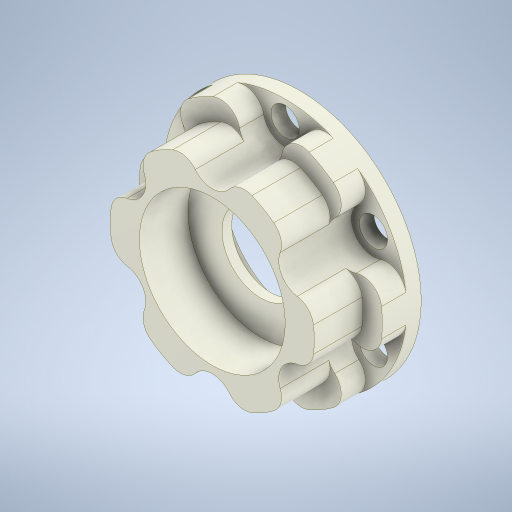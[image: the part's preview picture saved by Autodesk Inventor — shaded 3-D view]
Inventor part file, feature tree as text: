
AUTODESK INVENTOR PART (.ipt)
format: ipt  version: 2023.1 (Build 271208000, 208)  size: 422,400 bytes
history: native  units: mm
features: sketch x7, extrude x6, hole x1, fillet x1, pattern_circular x1
ambient origin geometry x8: Origin, YZ Plane, XZ Plane, XY Plane, X Axis, Y Axis, Z Axis, Center Point
bodies: Solid1 (feature_tree)
feature tree (16):
  extrude  "Extrusion1"  Depth=9.5mm TaperAngle=0.0deg
  hole  "Hole1"  [1 undecoded]
  extrude  "Extrusion2"  Depth=9.5mm
  extrude  "Extrusion3"  Depth=3.0mm
  extrude  "Extrusion4"  Depth=5.5mm TaperAngle=0.0deg
  extrude  "Extrusion5"  TaperAngle=0.0deg  [1 undecoded]
  fillet  "Fillet1"  Radius=2.0mm
  pattern_circular  "Circular Pattern1"  Count=6 Angle=360.0deg
  extrude  "Extrusion6"  [1 undecoded]
  sketch  "Sketch1"  dims[d0=25.0mm d1=9.5mm d2=0.0mm]
  sketch  "Sketch2"  dims[d3=10.5mm d4=60.0mm d6=360.0deg]
  sketch  "Sketch3"  dims[d8=2.9mm d9=4.4mm d10=4.5mm d11=8.0mm d12=90.0deg d13=9.5mm d14=0.0mm d15=15.5mm]
  sketch  "Sketch4"  dims[d16=3.0mm d17=0.0mm d18=15.0mm]
  sketch  "Sketch5"  dims[d19=5.5mm d20=0.0mm d21=5.5mm d22=0.0mm]
  sketch  "Sketch6"  dims[d23=8.0mm d24=0.0mm d25=0.0mm d26=2.0mm d27=60.0mm d28=360.0deg]
  sketch  "Sketch7"  dims[d30=0.5mm d31=0.0mm]
note: 3 required parameter values undecoded (feature->parameter linkage not recoverable at this tier; creation-order binding heuristic only, values carry confidence <= 0.55)
